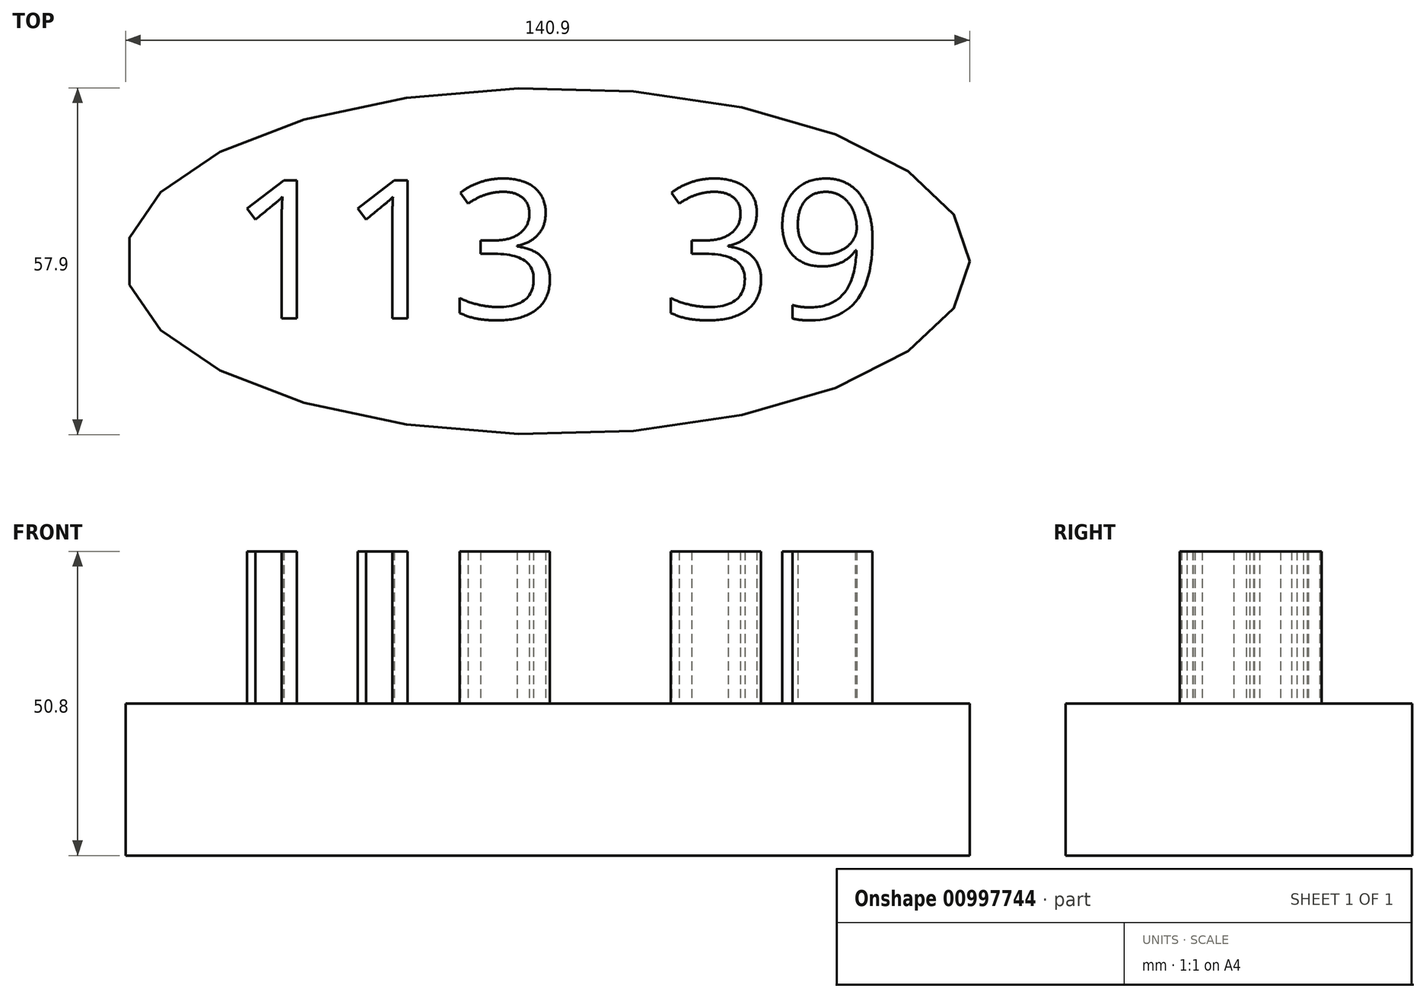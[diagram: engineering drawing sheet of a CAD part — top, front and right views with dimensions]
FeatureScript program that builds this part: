
annotation { "Feature Type Name" : "Feature", "Feature Type Description" : "" }
export const myFeature = defineFeature(function(context is Context, id is Id, definition is map)
    precondition{}
    {
        {
            var Q0;
            Q0=qCreatedBy(makeId("Top.planeOp"),FACE);
            var sketch = newSketch(context, id + "F0", { "sketchPlane" : qUnion([Q0])});
            skEllipse(sketch, "E0", {"center": v(0, 0) * mm, "majorRadius": 70.45 * mm, "minorRadius": 28.95 * mm, "majorAxis": v(1, 0)});
            skSolve(sketch);
        }
        {
            var Q0;
            Q0=makeQuery(id+"F0.imprint","IMPRINT",FACE,{"disambiguationData":[TD([[makeQuery(id+"F0.imprint","IMPRINT",EDGE,{"derivedFrom":sQuery(id+"F0.wireOp",EDGE,"E0")}),1.0]])]});
            extrude(context, id + "F1", {"entities" : qUnion([Q0]), "depth" : 25.4 * mm, "offsetDistance" : 25.4 * mm});
        }
        {
            var Q0;
            Q0=makeQuery(id+"F1.opExtrude","CAP_FACE",FACE,{"disambiguationData":[OSD([sQuery(id+"F0.wireOp",EDGE,"E0")])],"isStart":false});
            var sketch = newSketch(context, id + "F2", { "sketchPlane" : qUnion([Q0])});
            skText(sketch, "E1", { "text": "113  39", "fontName": "OpenSans-Regular.ttf"});
            const initialGuessF2  = {"E1": [-0.05311, -0.00956, 1, 0, 0.02325]};
            skSetInitialGuess(sketch, initialGuessF2);
            skSolve(sketch);
        }
        {
            var Q0;
            Q0 = qSketchRegion(id + "F2", true);
            extrude(context, id + "F3", {"entities" : qUnion([Q0]), "operationType" : NewBodyOperationType.ADD, "depth" : 25.4 * mm, "offsetDistance" : 25.4 * mm});
        }
    });
